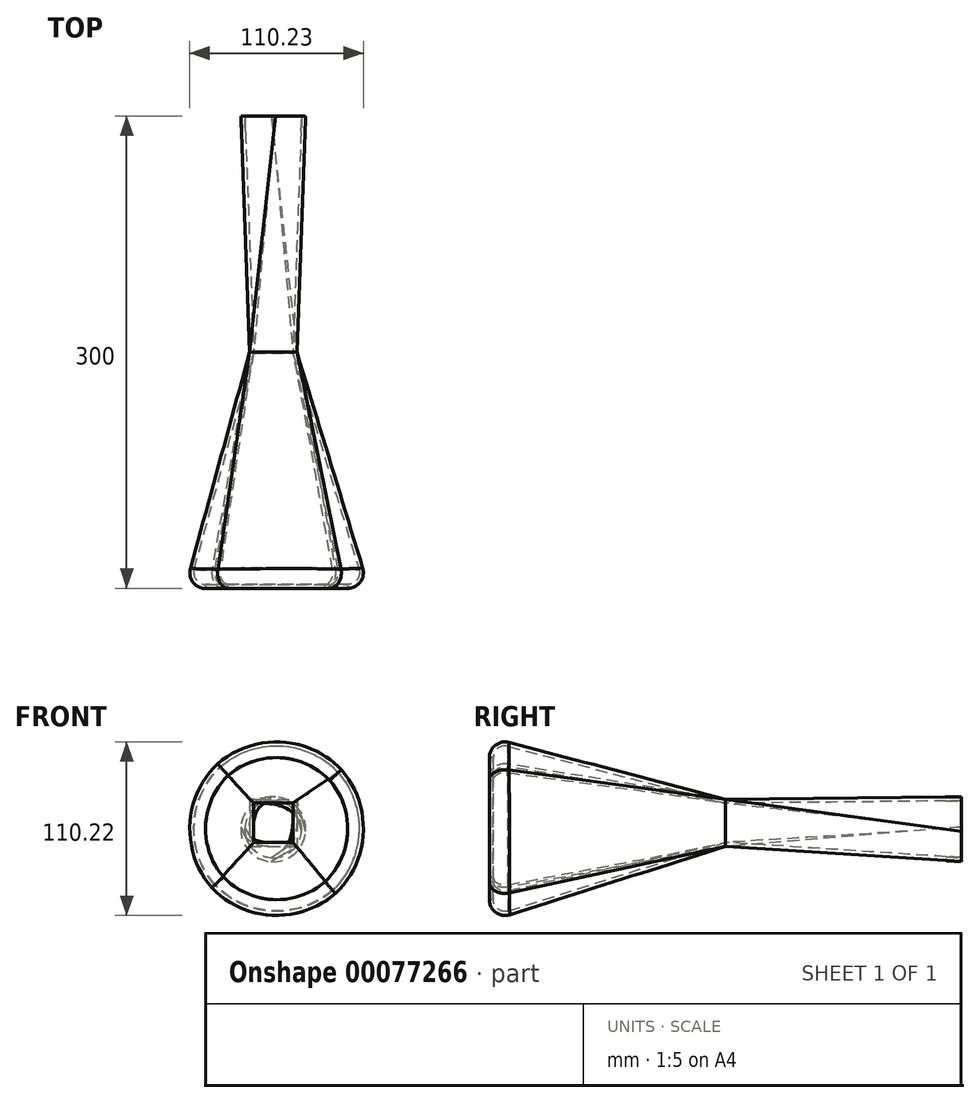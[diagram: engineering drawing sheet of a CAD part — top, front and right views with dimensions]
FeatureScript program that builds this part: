
annotation { "Feature Type Name" : "Feature", "Feature Type Description" : "" }
export const myFeature = defineFeature(function(context is Context, id is Id, definition is map)
    precondition{}
    {
        {
            var Q0;
            Q0=qCreatedBy(makeId("Front.planeOp"),FACE);
            var sketch = newSketch(context, id + "F0", { "sketchPlane" : qUnion([Q0])});
            skCircle(sketch, "E0", {"center": v(0, 0) * mm, "radius": 20.62 * mm});
            skPoint(sketch, "E1", {"position": v(0, -20.62) * mm});
            skPoint(sketch, "E2", {"position": v(20.57, -1.43) * mm});
            skPoint(sketch, "E3", {"position": v(1.39, 20.57) * mm});
            skPoint(sketch, "E4", {"position": v(-20.57, 1.31) * mm});
            skSolve(sketch);
        }
        {
            var Q0;
            Q0=qCreatedBy(makeId("Front.planeOp"),FACE);
            cPlane(context, id + "F1", {"entities" : qUnion([Q0]), "cplaneType" : CPlaneType.OFFSET, "offset" : 150 * mm, "width" : 150 * mm, "height" : 150 * mm});
        }
        {
            var Q0;
            Q0=qCreatedBy(id+"F1.planeOp",FACE);
            var sketch = newSketch(context, id + "F2", { "sketchPlane" : qUnion([Q0])});
            skLineSegment(sketch, "E5.bottom", {"start": v(-15, 19.06) * mm, "end": v(15, 19.06) * mm});
            skLineSegment(sketch, "E5.top", {"start": v(-15, -10.94) * mm, "end": v(15, -10.94) * mm});
            skLineSegment(sketch, "E5.left", {"start": v(-15, 19.06) * mm, "end": v(-15, -10.94) * mm});
            skLineSegment(sketch, "E5.right", {"start": v(15, 19.06) * mm, "end": v(15, -10.94) * mm});
            skPoint(sketch, "E5.middle", {"position": v(0, 4.06) * mm});
            skSolve(sketch);
        }
        {
            var Q0;
            Q0=makeQuery(id+"F0.imprint","IMPRINT",FACE,{"disambiguationData":[TD([[makeQuery(id+"F0.imprint","IMPRINT",EDGE,{"derivedFrom":sQuery(id+"F0.wireOp",EDGE,"E0")}),1.0]])]});
            var Q1;
            Q1=makeQuery(id+"F2.imprint","IMPRINT",FACE,{"disambiguationData":[TD([[makeQuery(id+"F2.imprint","IMPRINT",EDGE,{"derivedFrom":sQuery(id+"F2.wireOp",EDGE,"E5.bottom")}),-1.0]])]});
            var Q2;
            Q2=sQuery(id+"F0.wireOp",VERTEX,"E2");
            var Q3;
            Q3=sQuery(id+"F2.wireOp",VERTEX,"E5.right.start");
            loft(context, id + "F3", {"sheetProfilesArray" : [{ "sheetProfileEntities" : qUnion([Q0]) }, { "sheetProfileEntities" : qUnion([Q1]) }], "matchConnections" : true, "connections" : [{ "connectionEntities" : qUnion([Q2, Q3]), "connectionEdgeQueries" : qUnion([]), "connectionEdgeParameters" : [] }]});
        }
        {
            var Q0;
            Q0=qCreatedBy(id+"F1.planeOp",FACE);
            cPlane(context, id + "F4", {"entities" : qUnion([Q0]), "cplaneType" : CPlaneType.OFFSET, "offset" : 150 * mm, "width" : 150 * mm, "height" : 150 * mm});
        }
        {
            var Q0;
            Q0=qCreatedBy(id+"F4.planeOp",FACE);
            var sketch = newSketch(context, id + "F5", { "sketchPlane" : qUnion([Q0])});
            skCircle(sketch, "E6", {"center": v(2.28, 0) * mm, "radius": 58.42 * mm});
            skSolve(sketch);
        }
        {
            var Q1;
            Q1=makeQuery(id+"F3.opLoft","CAP_FACE",FACE,{"disambiguationData":[OSD([makeQuery(id+"F2.imprint","IMPRINT",FACE,{"disambiguationData":[TD([[makeQuery(id+"F2.imprint","IMPRINT",EDGE,{"derivedFrom":sQuery(id+"F2.wireOp",EDGE,"E5.bottom")}),-1.0]])]})])],"isStart":true});
            var Q2;
            Q2=makeQuery(id+"F5.imprint","IMPRINT",FACE,{"disambiguationData":[TD([[makeQuery(id+"F5.imprint","IMPRINT",EDGE,{"derivedFrom":sQuery(id+"F5.wireOp",EDGE,"E6")}),1.0]])]});
            loft(context, id + "F6", {"operationType" : NewBodyOperationType.ADD, "sheetProfilesArray" : [{ "sheetProfileEntities" : qUnion([Q1]) }, { "sheetProfileEntities" : qUnion([Q2]) }]});
        }
        {
            var Q0;
            Q0=makeQuery(id+"F6.opLoft","MID_CAP_EDGE",EDGE,{"disambiguationData":[OSD([sQuery(id+"F2.wireOp",EDGE,"E5.top"),sQuery(id+"F2.wireOp",EDGE,"E5.left"),sQuery(id+"F2.wireOp",EDGE,"E5.right"),sQuery(id+"F5.wireOp",EDGE,"E6")])],"capPos":1.0});
            var Q1;
            Q1=makeQuery(id+"F6.opLoft","MID_CAP_EDGE",EDGE,{"disambiguationData":[OSD([sQuery(id+"F2.wireOp",EDGE,"E5.bottom"),sQuery(id+"F2.wireOp",EDGE,"E5.top"),sQuery(id+"F2.wireOp",EDGE,"E5.left"),sQuery(id+"F2.wireOp",EDGE,"E5.right"),sQuery(id+"F5.wireOp",EDGE,"E6")])],"capPos":1.0});
            var Q2;
            Q2=makeQuery(id+"F6.opLoft","MID_CAP_EDGE",EDGE,{"disambiguationData":[OSD([sQuery(id+"F2.wireOp",EDGE,"E5.bottom"),sQuery(id+"F2.wireOp",EDGE,"E5.left"),sQuery(id+"F5.wireOp",EDGE,"E6")])],"capPos":1.0});
            var Q3;
            Q3=makeQuery(id+"F6.opLoft","MID_CAP_EDGE",EDGE,{"disambiguationData":[OSD([sQuery(id+"F2.wireOp",EDGE,"E5.bottom"),sQuery(id+"F2.wireOp",EDGE,"E5.top"),sQuery(id+"F2.wireOp",EDGE,"E5.left"),sQuery(id+"F5.wireOp",EDGE,"E6")])],"capPos":1.0});
            fillet(context, id + "F7", {"entities" : qUnion([Q0, Q1, Q2, Q3]), "radius" : 10 * mm, "tangentPropagation" : true, "allowEdgeOverflow" : false});
        }
        {
            var Q0;
            Q0=makeQuery(id+"F3.opLoft","CAP_FACE",FACE,{"disambiguationData":[OSD([makeQuery(id+"F0.imprint","IMPRINT",FACE,{"disambiguationData":[TD([[makeQuery(id+"F0.imprint","IMPRINT",EDGE,{"derivedFrom":sQuery(id+"F0.wireOp",EDGE,"E0")}),1.0]])]})])],"isStart":true});
            var Q1;
            Q1=makeQuery(id+"F6.opLoft","CAP_FACE",FACE,{"disambiguationData":[OSD([makeQuery(id+"F5.imprint","IMPRINT",FACE,{"disambiguationData":[TD([[makeQuery(id+"F5.imprint","IMPRINT",EDGE,{"derivedFrom":sQuery(id+"F5.wireOp",EDGE,"E6")}),1.0]])]})])],"isStart":true});
            shell(context, id + "F8", {"entities" : qUnion([Q0, Q1]), "thickness" : 2.5 * mm});
        }
    });
